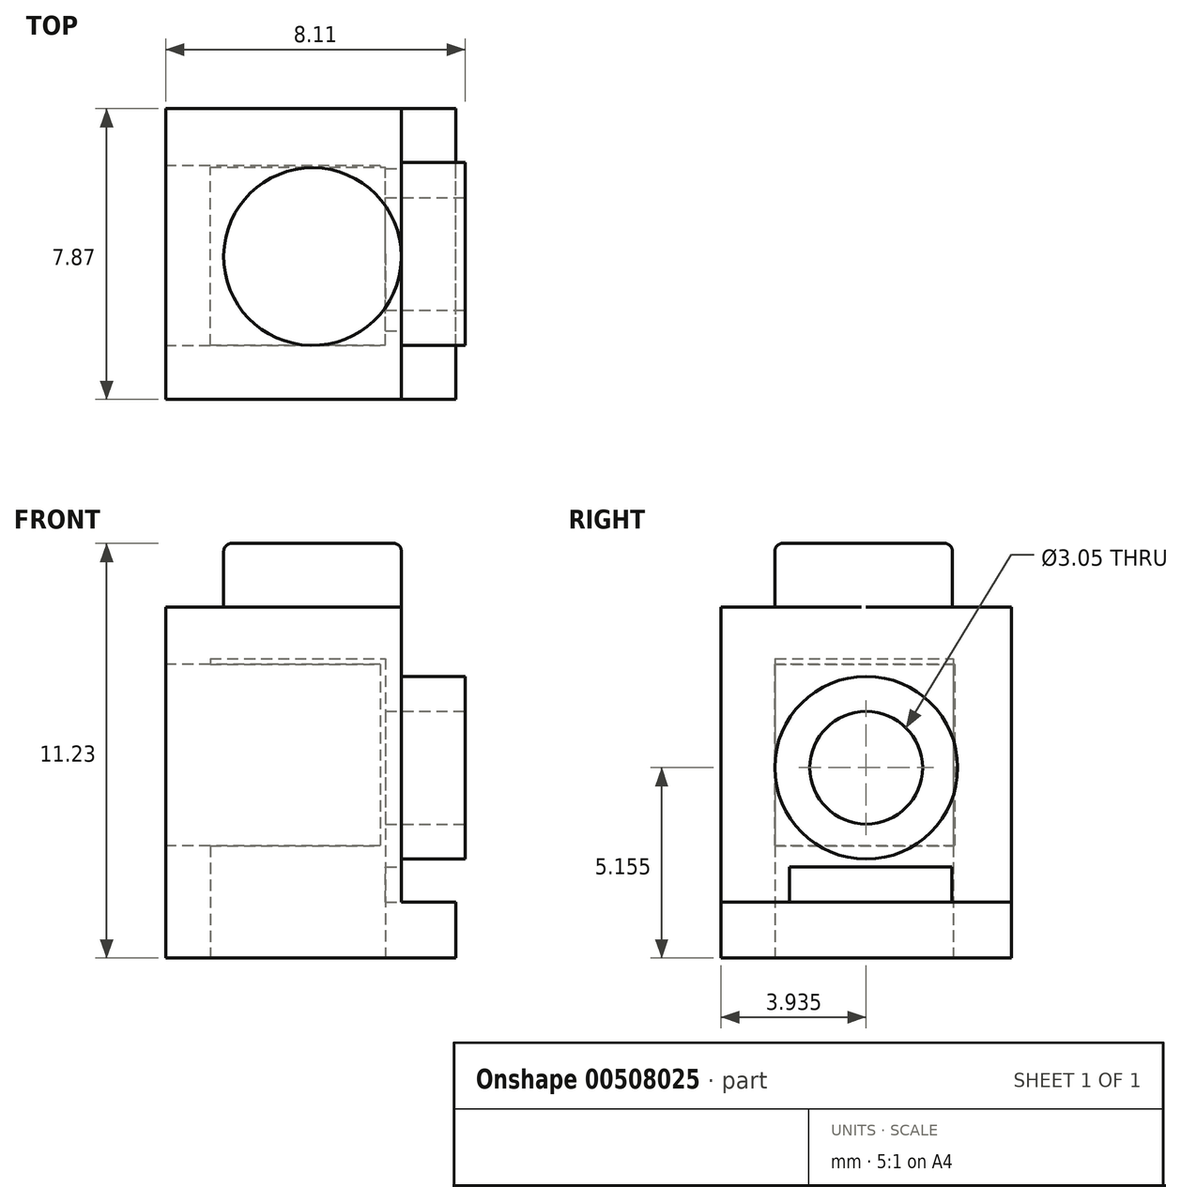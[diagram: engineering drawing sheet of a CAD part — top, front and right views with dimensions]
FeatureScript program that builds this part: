
annotation { "Feature Type Name" : "Feature", "Feature Type Description" : "" }
export const myFeature = defineFeature(function(context is Context, id is Id, definition is map)
    precondition{}
    {
        {
            var Q0;
            Q0=qCreatedBy(makeId("Front.planeOp"),FACE);
            var sketch = newSketch(context, id + "F0", { "sketchPlane" : qUnion([Q0])});
            skLineSegment(sketch, "E0", {"start": v(-34.46, 33.1) * mm, "end": v(-34.46, 23.6) * mm});
            skLineSegment(sketch, "E1", {"start": v(-34.46, 23.6) * mm, "end": v(-26.61, 23.6) * mm});
            skLineSegment(sketch, "E2", {"start": v(-26.61, 23.6) * mm, "end": v(-26.61, 25.12) * mm});
            skLineSegment(sketch, "E3", {"start": v(-26.61, 25.12) * mm, "end": v(-28.08, 25.12) * mm});
            skLineSegment(sketch, "E4", {"start": v(-28.08, 25.12) * mm, "end": v(-28.08, 33.1) * mm});
            skLineSegment(sketch, "E5", {"start": v(-28.08, 33.1) * mm, "end": v(-34.46, 33.1) * mm});
            skSolve(sketch);
        }
        {
            var Q0;
            Q0 = qSketchRegion(id + "F0", true);
            extrude(context, id + "F1", {"entities" : qUnion([Q0]), "depth" : 7.87 * mm, "offsetDistance" : 25 * mm});
        }
        {
            var Q0;
            Q0=makeQuery(id+"F1.opExtrude","SWEPT_FACE",FACE,{"disambiguationData":[OSD([sQuery(id+"F0.wireOp",EDGE,"E0")])]});
            var sketch = newSketch(context, id + "F2", { "sketchPlane" : qUnion([Q0])});
            skLineSegment(sketch, "E6.bottom", {"start": v(1.54, 31.55) * mm, "end": v(6.42, 31.55) * mm});
            skLineSegment(sketch, "E6.top", {"start": v(1.54, 26.64) * mm, "end": v(6.42, 26.64) * mm});
            skLineSegment(sketch, "E6.left", {"start": v(1.54, 31.55) * mm, "end": v(1.54, 26.64) * mm});
            skLineSegment(sketch, "E6.right", {"start": v(6.42, 31.55) * mm, "end": v(6.42, 26.64) * mm});
            skSolve(sketch);
        }
        {
            var Q0;
            Q0=makeQuery(id+"F2.imprint","IMPRINT",FACE,{"disambiguationData":[TD([[makeQuery(id+"F2.imprint","IMPRINT",EDGE,{"derivedFrom":sQuery(id+"F2.wireOp",EDGE,"E6.bottom")}),-1.0]])]});
            extrude(context, id + "F3", {"entities" : qUnion([Q0]), "operationType" : NewBodyOperationType.REMOVE, "oppositeDirection" : true, "depth" : 5.8 * mm, "offsetDistance" : 25 * mm});
        }
        {
            var Q0;
            Q0=makeQuery(id+"F1.opExtrude","SWEPT_FACE",FACE,{"disambiguationData":[OSD([sQuery(id+"F0.wireOp",EDGE,"E4")])]});
            var sketch = newSketch(context, id + "F4", { "sketchPlane" : qUnion([Q0])});
            skLineSegment(sketch, "E7.bottom", {"start": v(-6, 25.12) * mm, "end": v(-1.62, 25.12) * mm});
            skLineSegment(sketch, "E7.top", {"start": v(-6, 26.07) * mm, "end": v(-1.62, 26.07) * mm});
            skLineSegment(sketch, "E7.left", {"start": v(-6, 25.12) * mm, "end": v(-6, 26.07) * mm});
            skLineSegment(sketch, "E7.right", {"start": v(-1.62, 25.12) * mm, "end": v(-1.62, 26.07) * mm});
            skSolve(sketch);
        }
        {
            var Q0;
            Q0=makeQuery(id+"F4.imprint","IMPRINT",FACE,{"disambiguationData":[TD([[makeQuery(id+"F4.imprint","IMPRINT",EDGE,{"derivedFrom":sQuery(id+"F4.wireOp",EDGE,"E7.bottom")}),1.0]])]});
            extrude(context, id + "F5", {"entities" : qUnion([Q0]), "operationType" : NewBodyOperationType.REMOVE, "oppositeDirection" : true, "depth" : 1.95 * mm, "offsetDistance" : 25 * mm});
        }
        {
            var Q0;
            Q0=makeQuery(id+"F1.opExtrude","SWEPT_FACE",FACE,{"disambiguationData":[OSD([sQuery(id+"F0.wireOp",EDGE,"E1")])]});
            var sketch = newSketch(context, id + "F6", { "sketchPlane" : qUnion([Q0])});
            skLineSegment(sketch, "E8.bottom", {"start": v(-33.26, 6.4) * mm, "end": v(-28.52, 6.4) * mm});
            skLineSegment(sketch, "E8.top", {"start": v(-33.26, 1.58) * mm, "end": v(-28.52, 1.58) * mm});
            skLineSegment(sketch, "E8.left", {"start": v(-33.26, 6.4) * mm, "end": v(-33.26, 1.58) * mm});
            skLineSegment(sketch, "E8.right", {"start": v(-28.52, 6.4) * mm, "end": v(-28.52, 1.58) * mm});
            skSolve(sketch);
        }
        {
            var Q0;
            Q0 = qSketchRegion(id + "F6", true);
            var Q1;
            Q1=makeQuery(id+"F6.imprint","IMPRINT",FACE,{"disambiguationData":[TD([[makeQuery(id+"F6.imprint","IMPRINT",EDGE,{"derivedFrom":sQuery(id+"F6.wireOp",EDGE,"E8.bottom")}),-1.0]])]});
            extrude(context, id + "F7", {"entities" : qUnion([Q0, Q1]), "operationType" : NewBodyOperationType.REMOVE, "oppositeDirection" : true, "depth" : 8.1 * mm, "offsetDistance" : 25 * mm});
        }
        {
            var Q0;
            Q0=makeQuery(id+"F1.opExtrude","SWEPT_FACE",FACE,{"disambiguationData":[OSD([sQuery(id+"F0.wireOp",EDGE,"E4")])]});
            var sketch = newSketch(context, id + "F8", { "sketchPlane" : qUnion([Q0])});
            skCircle(sketch, "E9", {"center": v(-3.94, 28.76) * mm, "radius": 2.48 * mm});
            skPoint(sketch, "E9.centerSnap1", {"position": v(-3.94, 33.1) * mm});
            skSolve(sketch);
        }
        {
            var Q0;
            Q0 = qSketchRegion(id + "F8", true);
            extrude(context, id + "F9", {"entities" : qUnion([Q0]), "operationType" : NewBodyOperationType.ADD, "depth" : 1.73 * mm, "offsetDistance" : 25 * mm});
        }
        {
            var Q0;
            Q0=makeQuery(id+"F9.opExtrude","CAP_FACE",FACE,{"disambiguationData":[OSD([sQuery(id+"F8.wireOp",EDGE,"E9")])],"isStart":false});
            var sketch = newSketch(context, id + "F10", { "sketchPlane" : qUnion([Q0])});
            skCircle(sketch, "E10", {"center": v(-3.94, 28.76) * mm, "radius": 1.52 * mm});
            skSolve(sketch);
        }
        {
            var Q0;
            Q0=makeQuery(id+"F10.imprint","IMPRINT",FACE,{"disambiguationData":[TD([[makeQuery(id+"F10.imprint","IMPRINT",EDGE,{"derivedFrom":sQuery(id+"F10.wireOp",EDGE,"E10")}),1.0]])]});
            extrude(context, id + "F11", {"entities" : qUnion([Q0]), "operationType" : NewBodyOperationType.REMOVE, "oppositeDirection" : true, "depth" : 25 * mm, "offsetDistance" : 25 * mm});
        }
        {
            var Q0;
            Q0=makeQuery(id+"F1.opExtrude","SWEPT_FACE",FACE,{"disambiguationData":[OSD([sQuery(id+"F0.wireOp",EDGE,"E5")])]});
            var sketch = newSketch(context, id + "F12", { "sketchPlane" : qUnion([Q0])});
            skCircle(sketch, "E11", {"center": v(-30.49, -4) * mm, "radius": 2.4 * mm});
            skSolve(sketch);
        }
        {
            var Q0;
            Q0 = qSketchRegion(id + "F12", true);
            var Q1;
            {var subQ0=sQuery(id+"F12.wireOp",EDGE,"E11");var subQ1=makeQuery(id+"F1.opExtrude","SWEPT_EDGE",EDGE,{"disambiguationData":[OSD([sQuery(id+"F0.wireOp",EDGE,"E4"),sQuery(id+"F0.wireOp",EDGE,"E5")])]});var subQ2=makeQuery(id+"F12.imprint","INTERSECT",VERTEX,{"disambiguationData":[OD(0.0)],"derivedFrom":[subQ1,subQ0]});Q1=makeQuery(id+"F12.imprint","IMPRINT",FACE,{"disambiguationData":[TD([[makeQuery(id+"F12.imprint","IMPRINT",EDGE,{"disambiguationData":[TD([[subQ2,-1.0]])],"derivedFrom":subQ0}),1.0]])]});}
            extrude(context, id + "F13", {"entities" : qUnion([Q0, Q1]), "operationType" : NewBodyOperationType.ADD, "depth" : 1.73 * mm, "offsetDistance" : 25 * mm});
        }
        {
            var Q0;
            Q0=makeQuery(id+"F13.opExtrude","CAP_EDGE",EDGE,{"disambiguationData":[OSD([sQuery(id+"F12.wireOp",EDGE,"E11")])],"isStart":false});
            fillet(context, id + "F14", {"entities" : qUnion([Q0]), "radius" : 0.22 * mm, "tangentPropagation" : true, "allowEdgeOverflow" : false});
        }
    });
